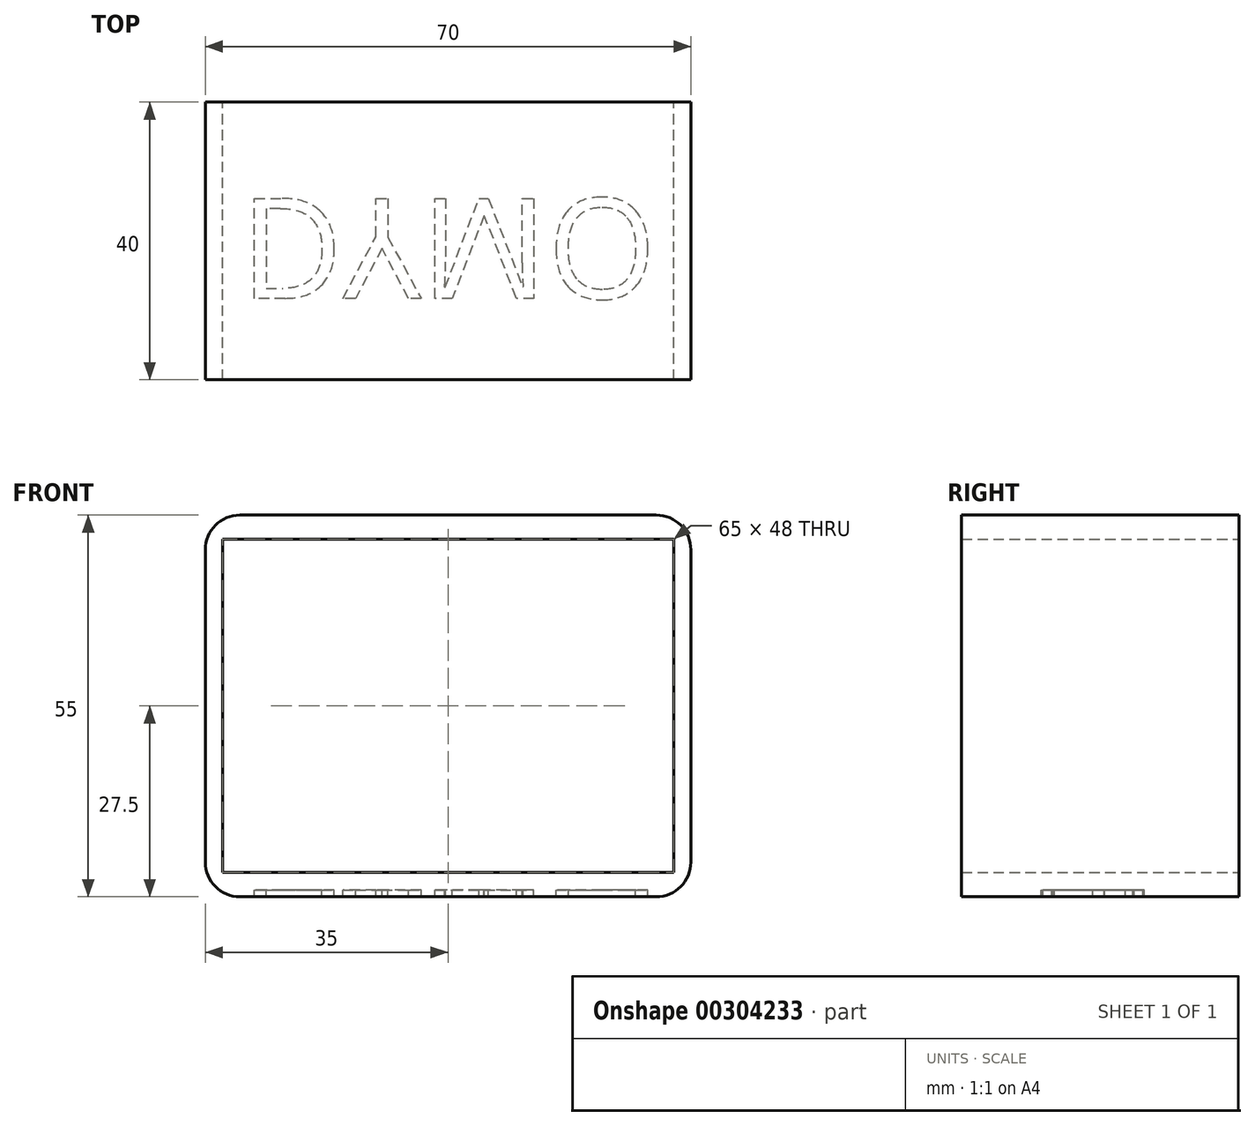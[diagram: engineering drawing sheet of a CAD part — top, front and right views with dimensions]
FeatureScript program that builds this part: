
annotation { "Feature Type Name" : "Feature", "Feature Type Description" : "" }
export const myFeature = defineFeature(function(context is Context, id is Id, definition is map)
    precondition{}
    {
        {
            var Q0;
            Q0=qCreatedBy(makeId("Front.planeOp"),FACE);
            var sketch = newSketch(context, id + "F0", { "sketchPlane" : qUnion([Q0])});
            skLineSegment(sketch, "E0.bottom", {"start": v(32.5, -24) * mm, "end": v(-32.5, -24) * mm});
            skLineSegment(sketch, "E0.top", {"start": v(32.5, 24) * mm, "end": v(-32.5, 24) * mm});
            skLineSegment(sketch, "E0.left", {"start": v(32.5, -24) * mm, "end": v(32.5, 24) * mm});
            skLineSegment(sketch, "E0.right", {"start": v(-32.5, -24) * mm, "end": v(-32.5, 24) * mm});
            skPoint(sketch, "E0.middle", {"position": v(0, 0) * mm});
            skLineSegment(sketch, "E1.bottom", {"start": v(35, -27.5) * mm, "end": v(-35, -27.5) * mm});
            skLineSegment(sketch, "E1.top", {"start": v(35, 27.5) * mm, "end": v(-35, 27.5) * mm});
            skLineSegment(sketch, "E1.left", {"start": v(35, -27.5) * mm, "end": v(35, 27.5) * mm});
            skLineSegment(sketch, "E1.right", {"start": v(-35, -27.5) * mm, "end": v(-35, 27.5) * mm});
            skSolve(sketch);
        }
        {
            var Q0;
            Q0 = qSketchRegion(id + "F0", true);
            extrude(context, id + "F1", {"entities" : qUnion([Q0]), "endBound" : BoundingType.SYMMETRIC, "depth" : 40 * mm});
        }
        {
            var Q0;
            Q0=makeQuery(id+"F1.opExtrude","SWEPT_EDGE",EDGE,{"disambiguationData":[OSD([sQuery(id+"F0.wireOp",EDGE,"E1.bottom"),sQuery(id+"F0.wireOp",EDGE,"E1.right")])]});
            var Q1;
            Q1=makeQuery(id+"F1.opExtrude","SWEPT_EDGE",EDGE,{"disambiguationData":[OSD([sQuery(id+"F0.wireOp",EDGE,"E1.bottom"),sQuery(id+"F0.wireOp",EDGE,"E1.left")])]});
            var Q2;
            Q2=makeQuery(id+"F1.opExtrude","SWEPT_EDGE",EDGE,{"disambiguationData":[OSD([sQuery(id+"F0.wireOp",EDGE,"E1.top"),sQuery(id+"F0.wireOp",EDGE,"E1.left")])]});
            var Q3;
            Q3=makeQuery(id+"F1.opExtrude","SWEPT_EDGE",EDGE,{"disambiguationData":[OSD([sQuery(id+"F0.wireOp",EDGE,"E1.top"),sQuery(id+"F0.wireOp",EDGE,"E1.right")])]});
            fillet(context, id + "F2", {"entities" : qUnion([Q0, Q1, Q2, Q3]), "radius" : 5 * mm, "tangentPropagation" : true, "allowEdgeOverflow" : false});
        }
        {
            var Q0;
            Q0=makeQuery(id+"F1.opExtrude","SWEPT_FACE",FACE,{"disambiguationData":[OSD([sQuery(id+"F0.wireOp",EDGE,"E1.bottom")])]});
            var sketch = newSketch(context, id + "F3", { "sketchPlane" : qUnion([Q0])});
            skText(sketch, "E2", { "text": "DYMO", "fontName": "OpenSans-Regular.ttf"});
            const initialGuessF3  = {"E2": [-0.02988, -0.00612, 1, 0, 0.01452]};
            skSetInitialGuess(sketch, initialGuessF3);
            skSolve(sketch);
        }
        {
            var Q0;
            Q0 = qSketchRegion(id + "F3", true);
            extrude(context, id + "F4", {"entities" : qUnion([Q0]), "operationType" : NewBodyOperationType.REMOVE, "endBound" : BoundingType.SYMMETRIC, "depth" : 2 * mm});
        }
    });
